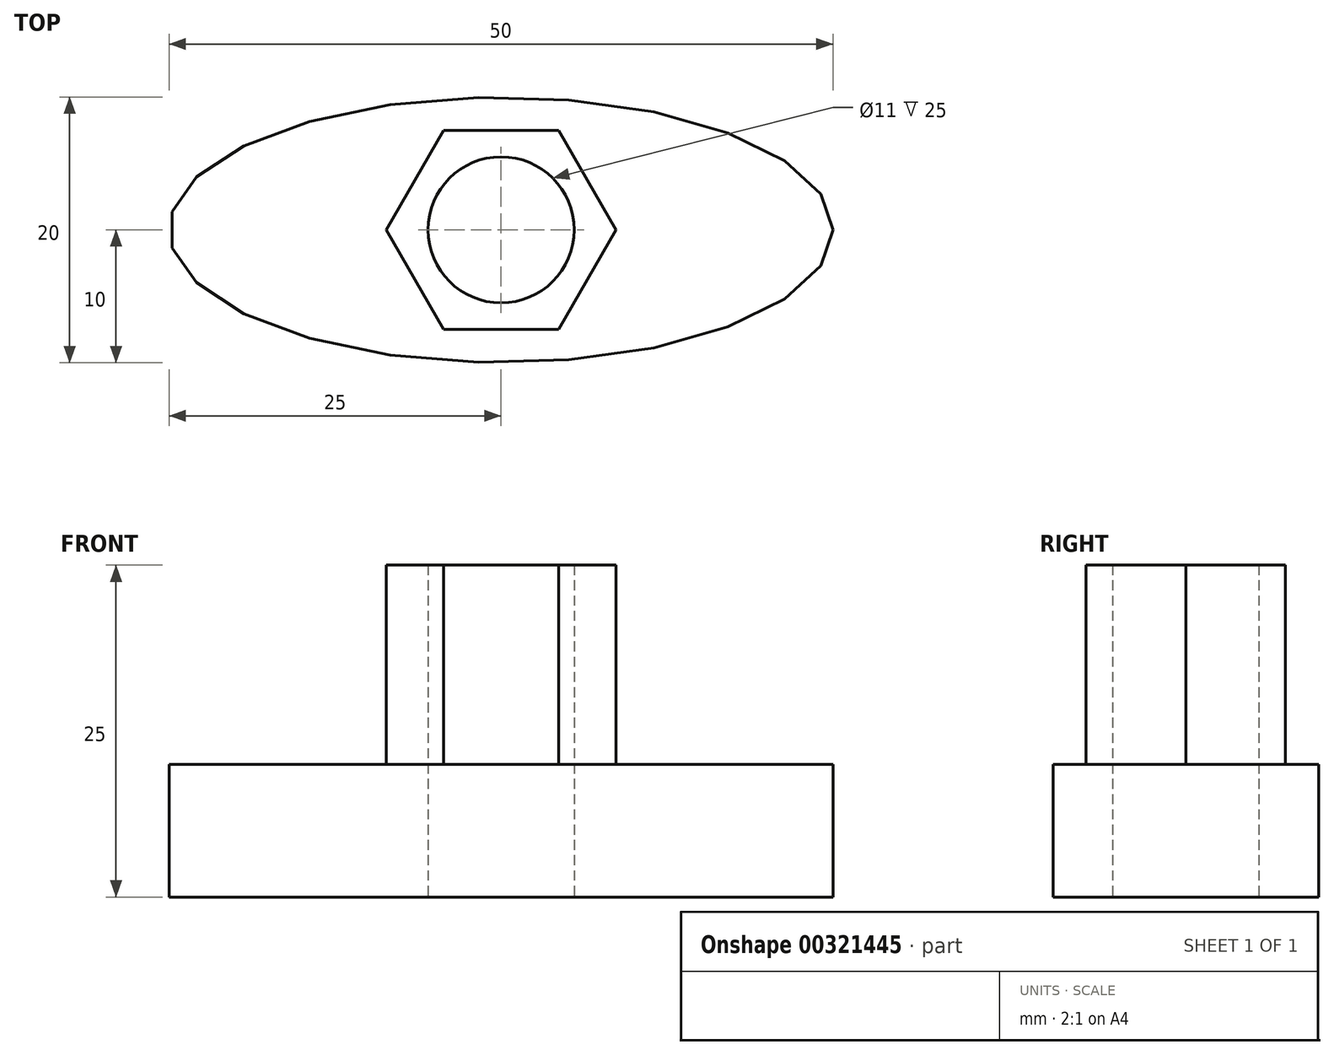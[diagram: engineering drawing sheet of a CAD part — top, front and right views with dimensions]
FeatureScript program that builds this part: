
annotation { "Feature Type Name" : "Feature", "Feature Type Description" : "" }
export const myFeature = defineFeature(function(context is Context, id is Id, definition is map)
    precondition{}
    {
        {
            var Q0;
            Q0=qCreatedBy(makeId("Top.planeOp"),FACE);
            var sketch = newSketch(context, id + "F0", { "sketchPlane" : qUnion([Q0])});
            skEllipse(sketch, "E0", {"center": v(0, 0) * mm, "majorRadius": 25 * mm, "minorRadius": 10 * mm, "majorAxis": v(1, 0)});
            skCircle(sketch, "E1", {"center": v(0, 0) * mm, "radius": 5.5 * mm});
            skSolve(sketch);
        }
        {
            var Q0;
            Q0 = qSketchRegion(id + "F0", true);
            extrude(context, id + "F1", {"entities" : qUnion([Q0]), "depth" : 10 * mm});
        }
        {
            var Q0;
            Q0=makeQuery(id+"F1.opExtrude","CAP_FACE",FACE,{"disambiguationData":[OSD([sQuery(id+"F0.wireOp",EDGE,"E0"),sQuery(id+"F0.wireOp",EDGE,"E1")])],"isStart":false});
            var sketch = newSketch(context, id + "F2", { "sketchPlane" : qUnion([Q0])});
            skCircle(sketch, "E2.cCircle", {"center": v(0, 0) * mm, "radius": 7.5 * mm, "construction": true});
            skLineSegment(sketch, "E2.0", {"start": v(8.66, 0) * mm, "end": v(4.33, -7.5) * mm});
            skLineSegment(sketch, "E2.1", {"start": v(4.33, -7.5) * mm, "end": v(-4.33, -7.5) * mm});
            skLineSegment(sketch, "E2.2", {"start": v(-4.33, -7.5) * mm, "end": v(-8.66, 0) * mm});
            skLineSegment(sketch, "E2.3", {"start": v(-8.66, 0) * mm, "end": v(-4.33, 7.5) * mm});
            skLineSegment(sketch, "E2.4", {"start": v(-4.33, 7.5) * mm, "end": v(4.33, 7.5) * mm});
            skLineSegment(sketch, "E2.5", {"start": v(4.33, 7.5) * mm, "end": v(8.66, 0) * mm});
            skPoint(sketch, "E2.0.midPoint", {"position": v(6.5, -3.75) * mm});
            skCircle(sketch, "E3", {"center": v(0, 0) * mm, "radius": 5.5 * mm});
            skSolve(sketch);
        }
        {
            var Q0;
            Q0 = qSketchRegion(id + "F2", true);
            extrude(context, id + "F3", {"entities" : qUnion([Q0]), "operationType" : NewBodyOperationType.ADD, "depth" : 15 * mm});
        }
    });
